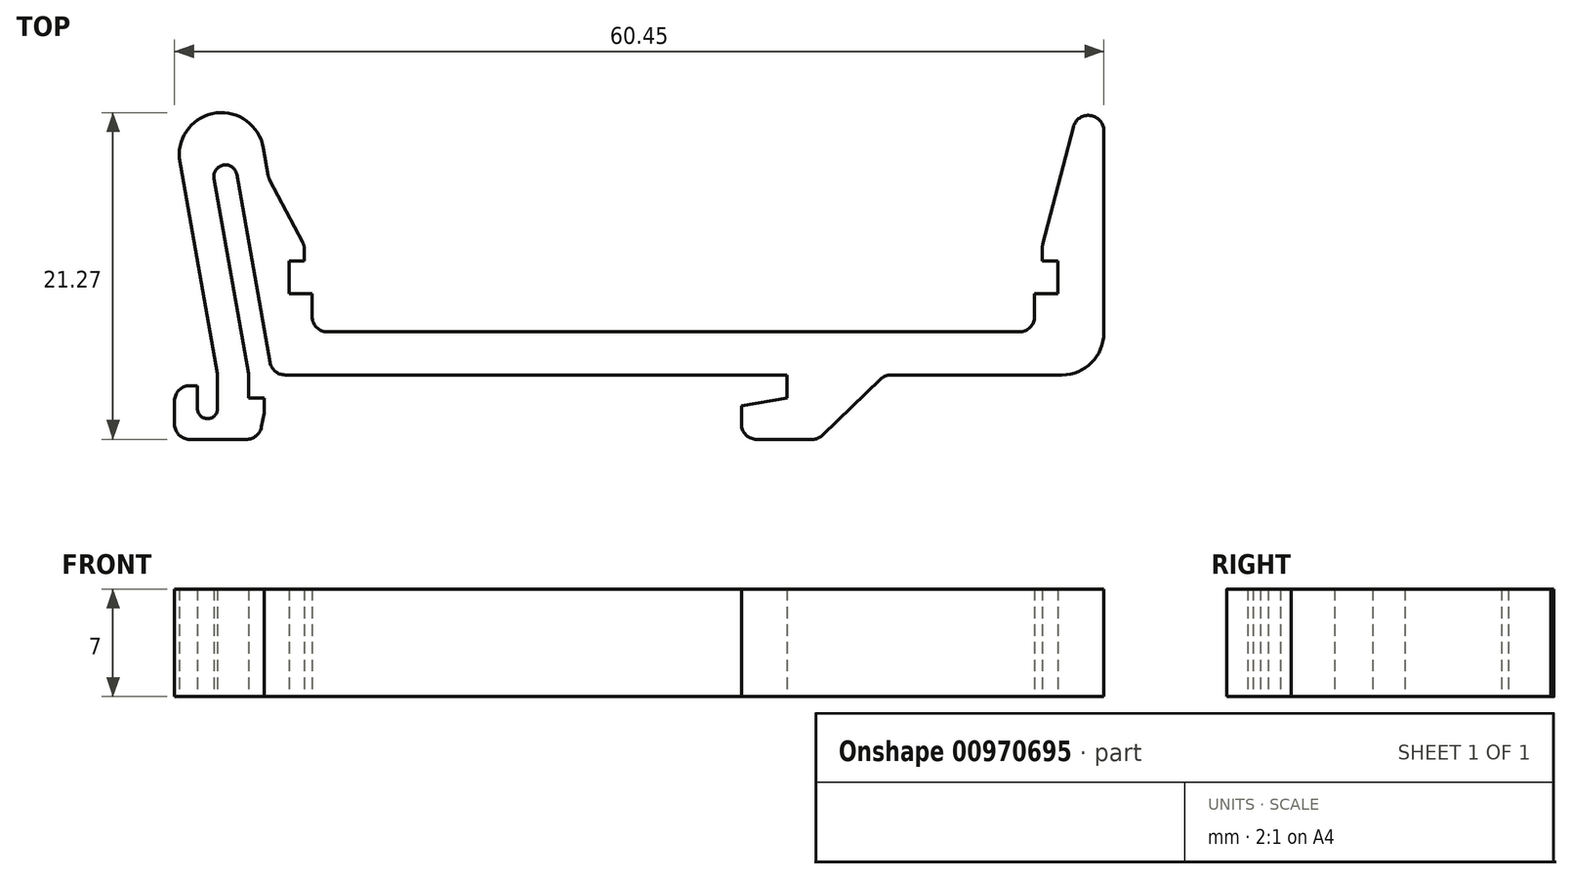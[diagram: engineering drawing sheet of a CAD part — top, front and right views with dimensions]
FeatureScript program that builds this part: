
annotation { "Feature Type Name" : "Feature", "Feature Type Description" : "" }
export const myFeature = defineFeature(function(context is Context, id is Id, definition is map)
    precondition{}
    {
        {
            var Q0;
            Q0=qCreatedBy(makeId("Top.planeOp"),FACE);
            var sketch = newSketch(context, id + "F0", { "sketchPlane" : qUnion([Q0])});
            skLineSegment(sketch, "E0", {"start": v(-27.83, -12.83) * mm, "end": v(-27.83, -9.33) * mm});
            skLineSegment(sketch, "E1", {"start": v(-27.83, -9.33) * mm, "end": v(-26.33, -9.33) * mm});
            skLineSegment(sketch, "E2", {"start": v(-26.33, -9.33) * mm, "end": v(-26.33, -10.83) * mm});
            skLineSegment(sketch, "E3", {"start": v(-25.26, 4.16) * mm, "end": v(-23, -8.63) * mm});
            skLineSegment(sketch, "E4", {"start": v(-23, -8.63) * mm, "end": v(-23, -10.13) * mm});
            skLineSegment(sketch, "E5", {"start": v(-22, -10.13) * mm, "end": v(-23, -10.13) * mm});
            skLineSegment(sketch, "E6", {"start": v(-27.83, -12.83) * mm, "end": v(-22.33, -12.83) * mm});
            skLineSegment(sketch, "E7", {"start": v(-19.38, -0.23) * mm, "end": v(-19.38, -1.23) * mm});
            skLineSegment(sketch, "E8", {"start": v(-19.38, -1.23) * mm, "end": v(-20.38, -1.23) * mm});
            skLineSegment(sketch, "E9", {"start": v(-20.38, -1.23) * mm, "end": v(-20.38, -3.33) * mm});
            skLineSegment(sketch, "E10", {"start": v(-20.38, -3.33) * mm, "end": v(-18.88, -3.33) * mm});
            skLineSegment(sketch, "E11", {"start": v(-18.88, -3.33) * mm, "end": v(-18.88, -5.83) * mm});
            skLineSegment(sketch, "E12", {"start": v(-18.88, -5.83) * mm, "end": v(18.4, -5.83) * mm});
            skLineSegment(sketch, "E13", {"start": v(-23.78, 4.42) * mm, "end": v(-21.48, -8.63) * mm});
            skLineSegment(sketch, "E14", {"start": v(-21.48, -8.63) * mm, "end": v(12, -8.63) * mm});
            skLineSegment(sketch, "E15", {"start": v(12, -8.63) * mm, "end": v(12, -10.13) * mm});
            skLineSegment(sketch, "E16", {"start": v(12, -10.13) * mm, "end": v(9.04, -10.63) * mm});
            skLineSegment(sketch, "E17", {"start": v(9.04, -12.83) * mm, "end": v(14.04, -12.83) * mm});
            skLineSegment(sketch, "E18", {"start": v(28.12, -5.83) * mm, "end": v(28.12, -3.33) * mm});
            skLineSegment(sketch, "E19", {"start": v(29.62, -3.33) * mm, "end": v(29.62, -1.23) * mm});
            skLineSegment(sketch, "E20", {"start": v(28.62, -1.23) * mm, "end": v(29.62, -1.23) * mm});
            skLineSegment(sketch, "E21", {"start": v(28.62, -1.23) * mm, "end": v(28.62, -0.23) * mm});
            skLineSegment(sketch, "E22", {"start": v(30.63, 7.5) * mm, "end": v(28.62, -0.23) * mm});
            skLineSegment(sketch, "E23", {"start": v(32.62, 7.25) * mm, "end": v(32.62, -5.9) * mm});
            skArc(sketch, "E24", {"start": v(-22.06, 6.16) * mm, "mid": v(-25.11, 8.42) * mm, "end": v(-27.52, 5.49) * mm});
            skLineSegment(sketch, "E25", {"start": v(28.12, -3.33) * mm, "end": v(29.62, -3.33) * mm});
            skArc(sketch, "E26", {"start": v(-23.78, 4.42) * mm, "mid": v(-24.65, 5.03) * mm, "end": v(-25.26, 4.16) * mm});
            skLineSegment(sketch, "E27", {"start": v(9.04, -10.63) * mm, "end": v(9.04, -12.83) * mm});
            skArc(sketch, "E28", {"start": v(32.62, 7.25) * mm, "mid": v(31.74, 8.25) * mm, "end": v(30.63, 7.5) * mm});
            skLineSegment(sketch, "E29", {"start": v(-22.06, 6.16) * mm, "end": v(-21.71, 4.2) * mm});
            skLineSegment(sketch, "E30", {"start": v(-21.71, 4.2) * mm, "end": v(-19.38, -0.23) * mm});
            skLineSegment(sketch, "E31", {"start": v(14.04, -12.83) * mm, "end": v(18.4, -8.63) * mm});
            skLineSegment(sketch, "E32", {"start": v(28.12, -5.83) * mm, "end": v(18.4, -5.83) * mm});
            skLineSegment(sketch, "E33", {"start": v(18.4, -5.83) * mm, "end": v(18.4, -8.63) * mm, "construction": true});
            skLineSegment(sketch, "E34", {"start": v(18.4, -8.63) * mm, "end": v(29.89, -8.63) * mm});
            skArc(sketch, "E35", {"start": v(29.89, -8.63) * mm, "mid": v(31.82, -7.84) * mm, "end": v(32.62, -5.9) * mm});
            skLineSegment(sketch, "E36", {"start": v(-25.03, -8.63) * mm, "end": v(-27.52, 5.49) * mm});
            skLineSegment(sketch, "E37", {"start": v(-25.03, -8.63) * mm, "end": v(-25.03, -10.83) * mm});
            skLineSegment(sketch, "E38", {"start": v(-22, -10.13) * mm, "end": v(-22, -11.13) * mm});
            skLineSegment(sketch, "E39", {"start": v(-22, -11.13) * mm, "end": v(-22.33, -12.83) * mm});
            skArc(sketch, "E40", {"start": v(-26.33, -10.83) * mm, "mid": v(-25.68, -11.48) * mm, "end": v(-25.03, -10.83) * mm});
            skSolve(sketch);
        }
        {
            var Q0;
            Q0=qSketchRegion(id+"F0",true);
            extrude(context, id + "F1", {"entities" : qUnion([Q0]), "depth" : 7 * mm});
        }
        {
            var Q0;
            Q0=makeQuery(id+"F1.opExtrude","SWEPT_EDGE",EDGE,{"disambiguationData":[OSD([sQuery(id+"F0.wireOp",EDGE,"E17"),sQuery(id+"F0.wireOp",EDGE,"E31")])]});
            var Q1;
            Q1=makeQuery(id+"F1.opExtrude","SWEPT_EDGE",EDGE,{"disambiguationData":[OSD([sQuery(id+"F0.wireOp",EDGE,"E0"),sQuery(id+"F0.wireOp",EDGE,"E6")])]});
            var Q2;
            Q2=makeQuery(id+"F1.opExtrude","SWEPT_EDGE",EDGE,{"disambiguationData":[OSD([sQuery(id+"F0.wireOp",EDGE,"E6"),sQuery(id+"F0.wireOp",EDGE,"E39")])]});
            var Q3;
            Q3=makeQuery(id+"F1.opExtrude","SWEPT_EDGE",EDGE,{"disambiguationData":[OSD([sQuery(id+"F0.wireOp",EDGE,"E36"),sQuery(id+"F0.wireOp",EDGE,"E37")])]});
            var Q4;
            Q4=makeQuery(id+"F1.opExtrude","SWEPT_EDGE",EDGE,{"disambiguationData":[OSD([sQuery(id+"F0.wireOp",EDGE,"E31"),sQuery(id+"F0.wireOp",EDGE,"E34")])]});
            var Q5;
            Q5=makeQuery(id+"F1.opExtrude","SWEPT_EDGE",EDGE,{"disambiguationData":[OSD([sQuery(id+"F0.wireOp",EDGE,"E17"),sQuery(id+"F0.wireOp",EDGE,"E27")])]});
            var Q6;
            Q6=makeQuery(id+"F1.opExtrude","SWEPT_EDGE",EDGE,{"disambiguationData":[OSD([sQuery(id+"F0.wireOp",EDGE,"E29"),sQuery(id+"F0.wireOp",EDGE,"E30")])]});
            var Q7;
            Q7=makeQuery(id+"F1.opExtrude","SWEPT_EDGE",EDGE,{"disambiguationData":[OSD([sQuery(id+"F0.wireOp",EDGE,"E21"),sQuery(id+"F0.wireOp",EDGE,"E22")])]});
            var Q8;
            Q8=makeQuery(id+"F1.opExtrude","SWEPT_EDGE",EDGE,{"disambiguationData":[OSD([sQuery(id+"F0.wireOp",EDGE,"E7"),sQuery(id+"F0.wireOp",EDGE,"E30")])]});
            var Q9;
            Q9=makeQuery(id+"F1.opExtrude","SWEPT_EDGE",EDGE,{"disambiguationData":[OSD([sQuery(id+"F0.wireOp",EDGE,"E11"),sQuery(id+"F0.wireOp",EDGE,"E12")])]});
            var Q10;
            Q10=makeQuery(id+"F1.opExtrude","SWEPT_EDGE",EDGE,{"disambiguationData":[OSD([sQuery(id+"F0.wireOp",EDGE,"E13"),sQuery(id+"F0.wireOp",EDGE,"E14")])]});
            var Q11;
            Q11=makeQuery(id+"F1.opExtrude","SWEPT_EDGE",EDGE,{"disambiguationData":[OSD([sQuery(id+"F0.wireOp",EDGE,"E18"),sQuery(id+"F0.wireOp",EDGE,"E32")])]});
            var Q12;
            Q12=makeQuery(id+"F1.opExtrude","SWEPT_EDGE",EDGE,{"disambiguationData":[OSD([sQuery(id+"F0.wireOp",EDGE,"E3"),sQuery(id+"F0.wireOp",EDGE,"E4")])]});
            var Q13;
            Q13=makeQuery(id+"F1.opExtrude","SWEPT_EDGE",EDGE,{"disambiguationData":[OSD([sQuery(id+"F0.wireOp",EDGE,"E36"),sQuery(id+"F0.wireOp",EDGE,"E37")])]});
            var Q14;
            Q14=makeQuery(id+"F1.opExtrude","SWEPT_EDGE",EDGE,{"disambiguationData":[OSD([sQuery(id+"F0.wireOp",EDGE,"E0"),sQuery(id+"F0.wireOp",EDGE,"E1")])]});
            fillet(context, id + "F2", {"entities" : qUnion([Q0, Q1, Q2, Q3, Q4, Q5, Q6, Q7, Q8, Q9, Q10, Q11, Q12, Q13, Q14]), "radius" : 1 * mm, "tangentPropagation" : true, "allowEdgeOverflow" : false});
        }
    });
